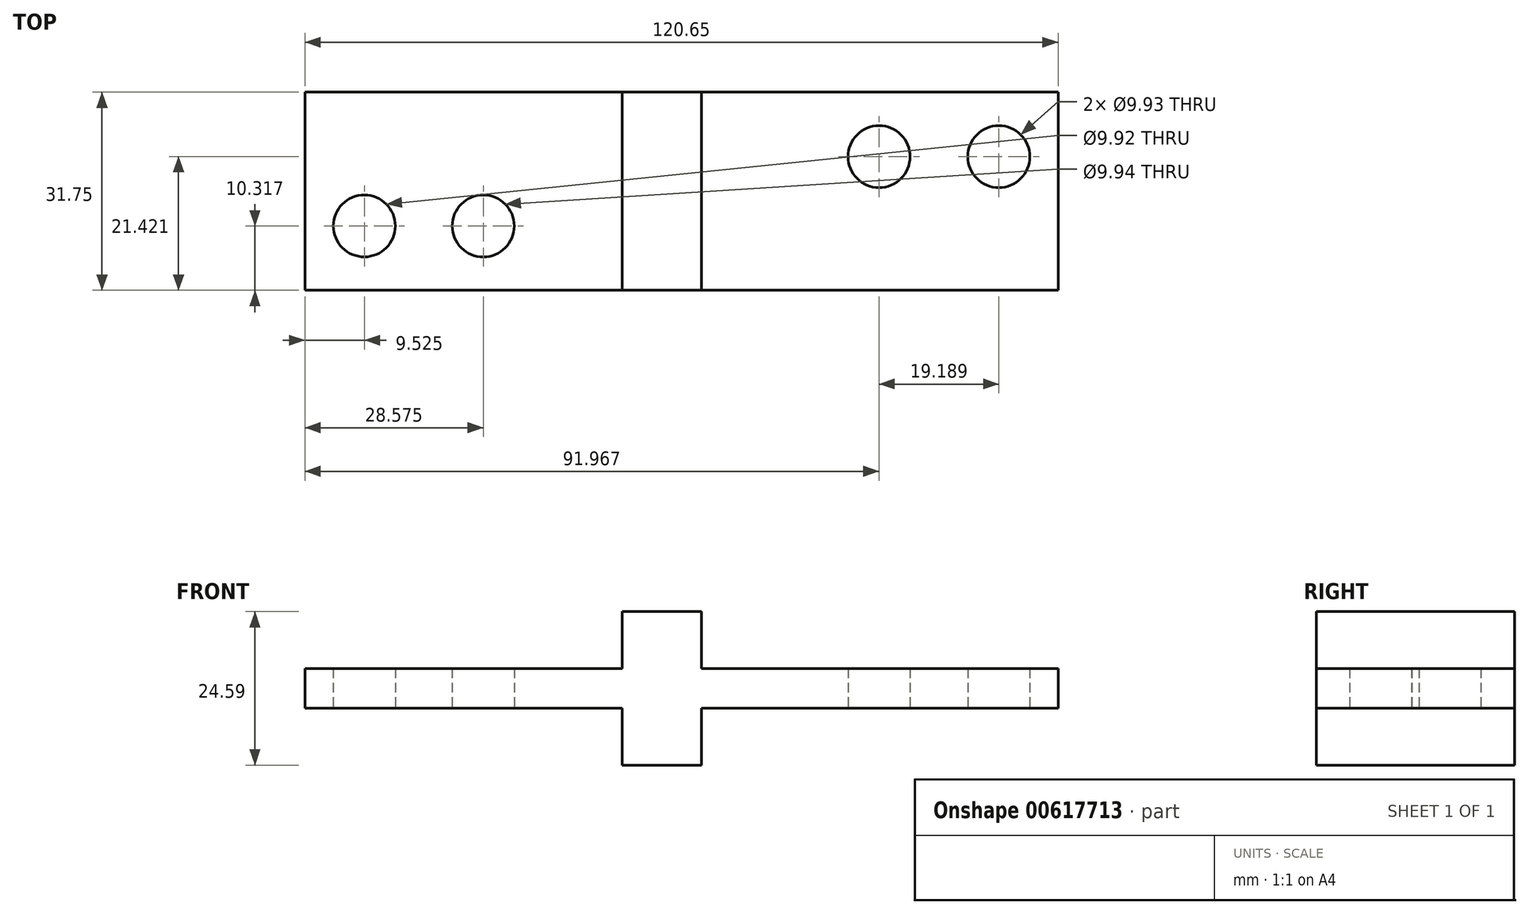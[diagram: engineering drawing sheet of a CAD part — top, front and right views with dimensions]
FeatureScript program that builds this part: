
annotation { "Feature Type Name" : "Feature", "Feature Type Description" : "" }
export const myFeature = defineFeature(function(context is Context, id is Id, definition is map)
    precondition{}
    {
        {
            var Q0;
            Q0=qCreatedBy(makeId("Front.planeOp"),FACE);
            var sketch = newSketch(context, id + "F0", { "sketchPlane" : qUnion([Q0])});
            skLineSegment(sketch, "E0", {"start": v(0, 0) * mm, "end": v(0, 6.35) * mm});
            skLineSegment(sketch, "E1", {"start": v(0, 6.35) * mm, "end": v(50.8, 6.35) * mm});
            skLineSegment(sketch, "E2", {"start": v(50.8, 6.35) * mm, "end": v(50.8, 15.47) * mm});
            skLineSegment(sketch, "E3", {"start": v(50.8, 15.47) * mm, "end": v(63.5, 15.47) * mm});
            skLineSegment(sketch, "E4", {"start": v(63.5, 15.47) * mm, "end": v(63.5, 6.35) * mm});
            skLineSegment(sketch, "E5", {"start": v(63.5, 6.35) * mm, "end": v(120.65, 6.35) * mm});
            skLineSegment(sketch, "E6", {"start": v(120.65, 6.35) * mm, "end": v(120.65, 0) * mm});
            skLineSegment(sketch, "E7", {"start": v(120.65, 0) * mm, "end": v(63.5, 0) * mm});
            skLineSegment(sketch, "E8", {"start": v(63.5, 0) * mm, "end": v(63.5, -9.12) * mm});
            skLineSegment(sketch, "E9", {"start": v(63.5, -9.12) * mm, "end": v(50.8, -9.12) * mm});
            skLineSegment(sketch, "E10", {"start": v(50.8, -9.12) * mm, "end": v(50.8, 0) * mm});
            skLineSegment(sketch, "E11", {"start": v(50.8, 0) * mm, "end": v(0, 0) * mm});
            skSolve(sketch);
        }
        {
            var Q0;
            Q0=makeQuery(id+"F0.imprint","IMPRINT",FACE,{"disambiguationData":[TD([[makeQuery(id+"F0.imprint","IMPRINT",EDGE,{"derivedFrom":sQuery(id+"F0.wireOp",EDGE,"E0")}),-1.0]])]});
            extrude(context, id + "F1", {"entities" : qUnion([Q0]), "depth" : 31.75 * mm, "offsetDistance" : 25.4 * mm});
        }
        {
            var Q0;
            Q0=qCreatedBy(makeId("Top.planeOp"),FACE);
            var sketch = newSketch(context, id + "F2", { "sketchPlane" : qUnion([Q0])});
            skCircle(sketch, "E12", {"center": v(9.52, -21.43) * mm, "radius": 4.96 * mm});
            skCircle(sketch, "E13", {"center": v(28.58, -21.43) * mm, "radius": 4.97 * mm});
            skCircle(sketch, "E14", {"center": v(111.16, -10.33) * mm, "radius": 4.97 * mm});
            skCircle(sketch, "E15", {"center": v(91.97, -10.33) * mm, "radius": 4.97 * mm});
            skSolve(sketch);
        }
        {
            var Q0;
            Q0=makeQuery(id+"F1.opExtrude","SWEPT_FACE",FACE,{"disambiguationData":[OSD([sQuery(id+"F0.wireOp",EDGE,"E5")])]});
            var Q1;
            Q1=makeQuery(id+"F2.imprint","IMPRINT",FACE,{"disambiguationData":[TD([[makeQuery(id+"F2.imprint","IMPRINT",EDGE,{"derivedFrom":sQuery(id+"F2.wireOp",EDGE,"E12")}),1.0]])]});
            var Q2;
            Q2=makeQuery(id+"F2.imprint","IMPRINT",FACE,{"disambiguationData":[TD([[makeQuery(id+"F2.imprint","IMPRINT",EDGE,{"derivedFrom":sQuery(id+"F2.wireOp",EDGE,"E13")}),1.0]])]});
            var Q3;
            Q3=makeQuery(id+"F2.imprint","IMPRINT",FACE,{"disambiguationData":[TD([[makeQuery(id+"F2.imprint","IMPRINT",EDGE,{"derivedFrom":sQuery(id+"F2.wireOp",EDGE,"E15")}),1.0]])]});
            var Q4;
            Q4=makeQuery(id+"F2.imprint","IMPRINT",FACE,{"disambiguationData":[TD([[makeQuery(id+"F2.imprint","IMPRINT",EDGE,{"derivedFrom":sQuery(id+"F2.wireOp",EDGE,"E14")}),1.0]])]});
            extrude(context, id + "F3", {"entities" : qUnion([Q0, Q1, Q2, Q3, Q4]), "operationType" : NewBodyOperationType.REMOVE, "depth" : 25.4 * mm, "offsetDistance" : 25.4 * mm});
        }
    });
